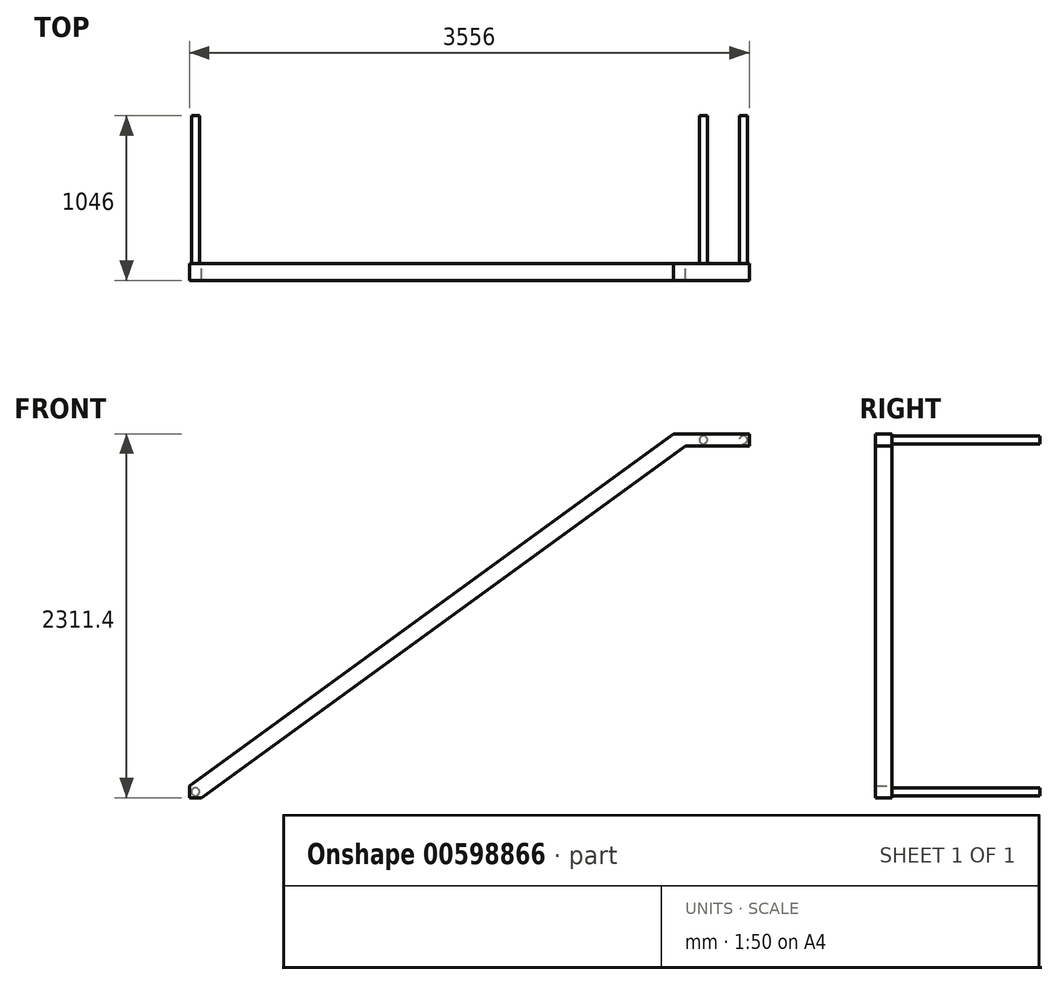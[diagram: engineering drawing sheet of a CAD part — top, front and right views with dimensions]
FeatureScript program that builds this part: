
annotation { "Feature Type Name" : "Feature", "Feature Type Description" : "" }
export const myFeature = defineFeature(function(context is Context, id is Id, definition is map)
    precondition{}
    {
        {
            var Q0;
            Q0=qCreatedBy(makeId("Front.planeOp"),FACE);
            var sketch = newSketch(context, id + "F0", { "sketchPlane" : qUnion([Q0])});
            skLineSegment(sketch, "E0", {"start": v(2064.45, 93.65) * mm, "end": v(1581.85, 93.65) * mm});
            skLineSegment(sketch, "E1", {"start": v(2064.45, 93.65) * mm, "end": v(2064.45, 17.45) * mm});
            skLineSegment(sketch, "E2", {"start": v(2064.45, 17.45) * mm, "end": v(1658.05, 17.45) * mm});
            skLineSegment(sketch, "E3", {"start": v(1658.05, 17.45) * mm, "end": v(-1415.35, -2217.75) * mm});
            skLineSegment(sketch, "E4", {"start": v(1581.85, 93.65) * mm, "end": v(-1491.55, -2141.55) * mm});
            skLineSegment(sketch, "E5", {"start": v(-1491.55, -2141.55) * mm, "end": v(-1491.55, -2217.75) * mm});
            skLineSegment(sketch, "E6", {"start": v(-1415.35, -2217.75) * mm, "end": v(-1491.55, -2217.75) * mm});
            skSolve(sketch);
        }
        {
            var Q0;
            Q0=makeQuery(id+"F0.imprint","IMPRINT",FACE,{"disambiguationData":[TD([[makeQuery(id+"F0.imprint","IMPRINT",EDGE,{"derivedFrom":sQuery(id+"F0.wireOp",EDGE,"E0")}),1.0]])]});
            extrude(context, id + "F1", {"entities" : qUnion([Q0]), "depth" : 106.2 * mm, "offsetDistance" : 25.4 * mm});
        }
        {
            var Q0;
            Q0=makeQuery(id+"F1.opExtrude","CAP_FACE",FACE,{"disambiguationData":[OSD([sQuery(id+"F0.wireOp",EDGE,"E0"),sQuery(id+"F0.wireOp",EDGE,"E1"),sQuery(id+"F0.wireOp",EDGE,"E2"),sQuery(id+"F0.wireOp",EDGE,"E3"),sQuery(id+"F0.wireOp",EDGE,"E4"),sQuery(id+"F0.wireOp",EDGE,"E5"),sQuery(id+"F0.wireOp",EDGE,"E6")])],"isStart":true});
            var sketch = newSketch(context, id + "F2", { "sketchPlane" : qUnion([Q0])});
            skLineSegment(sketch, "E7", {"start": v(-2064.45, 55.55) * mm, "end": v(-2026.35, 55.55) * mm});
            skCircle(sketch, "E8", {"center": v(-2026.35, 55.55) * mm, "radius": 25.4 * mm});
            skLineSegment(sketch, "E9", {"start": v(-2026.35, 55.55) * mm, "end": v(-1772.35, 55.55) * mm});
            skCircle(sketch, "E10", {"center": v(-1772.35, 55.55) * mm, "radius": 25.4 * mm});
            skLineSegment(sketch, "E11", {"start": v(1491.55, -2179.65) * mm, "end": v(1453.45, -2179.65) * mm});
            skCircle(sketch, "E12", {"center": v(1453.45, -2179.65) * mm, "radius": 25.4 * mm});
            skSolve(sketch);
        }
        {
            var Q0;
            Q0=makeQuery(id+"F2.imprint","IMPRINT",FACE,{"disambiguationData":[TD([[makeQuery(id+"F2.imprint","IMPRINT",EDGE,{"derivedFrom":sQuery(id+"F2.wireOp",EDGE,"E10")}),1.0]])]});
            var Q1;
            {var subQ0=sQuery(id+"F2.wireOp",EDGE,"E9");var subQ1=sQuery(id+"F2.wireOp",EDGE,"E7");var subQ2=makeQuery(id+"F2.imprint","INTERSECT",VERTEX,{"derivedFrom":[subQ1,subQ0]});Q1=makeQuery(id+"F2.imprint","IMPRINT",FACE,{"disambiguationData":[TD([[makeQuery(id+"F2.imprint","IMPRINT",EDGE,{"disambiguationData":[TD([[subQ2,1.0]])],"derivedFrom":subQ1}),1.0]])]});}
            var Q2;
            {var subQ0=sQuery(id+"F2.wireOp",EDGE,"E9");var subQ1=sQuery(id+"F2.wireOp",EDGE,"E7");var subQ2=makeQuery(id+"F2.imprint","INTERSECT",VERTEX,{"derivedFrom":[subQ1,subQ0]});Q2=makeQuery(id+"F2.imprint","IMPRINT",FACE,{"disambiguationData":[TD([[makeQuery(id+"F2.imprint","IMPRINT",EDGE,{"disambiguationData":[TD([[subQ2,1.0]])],"derivedFrom":subQ1}),-1.0]])]});}
            var Q3;
            Q3=makeQuery(id+"F2.imprint","IMPRINT",FACE,{"disambiguationData":[TD([[makeQuery(id+"F2.imprint","IMPRINT",EDGE,{"derivedFrom":sQuery(id+"F2.wireOp",EDGE,"E12")}),1.0]])]});
            extrude(context, id + "F3", {"entities" : qUnion([Q0, Q1, Q2, Q3]), "operationType" : NewBodyOperationType.ADD, "depth" : 939.8 * mm, "offsetDistance" : 25.4 * mm});
        }
    });
